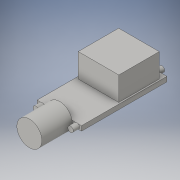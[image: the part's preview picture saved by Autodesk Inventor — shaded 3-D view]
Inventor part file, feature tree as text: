
AUTODESK INVENTOR PART (.ipt)
format: ipt  version: 2016 (Build 200138000, 138)  size: 155,648 bytes
history: native  units: in
note: dims shown in document units (in); Inventor stores cm internally (conversion verified against a paired STEP export)
features: extrude x5, sketch x5
ambient origin geometry x8: Origin, YZ Plane, XZ Plane, XY Plane, X Axis, Y Axis, Z Axis, Center Point
bodies: Solid1 (feature_tree)
feature tree (10):
  extrude  "Extrusion1"  Depth=0.711in
  extrude  "Extrusion2"  Depth=0.648in
  extrude  "Extrusion3"  Depth=0.024in
  extrude  "Extrusion4"  Depth=0.381in TaperAngle=0.0deg
  extrude  "Extrusion5"  Depth=0.486in TaperAngle=0.0deg
  sketch  "Sketch1"  dims[d0=1.369in d1=0.711in]
  sketch  "Sketch2"  dims[d2=0.076in d3=0.0in d4=0.648in]
  sketch  "Sketch3"  dims[d5=0.65in d6=0.024in]
  sketch  "Sketch4"  dims[d9=0.621in d10=0.381in d11=0.0in]
  sketch  "Sketch5"  dims[d12=0.4in d13=0.486in d14=0.0in d15=0.362in d16=0.181in d17=0.181in d18=0.088in d19=0.088in d20=0.088in d21=0.1in d22=0.0in d23=0.1in d24=0.0in]
